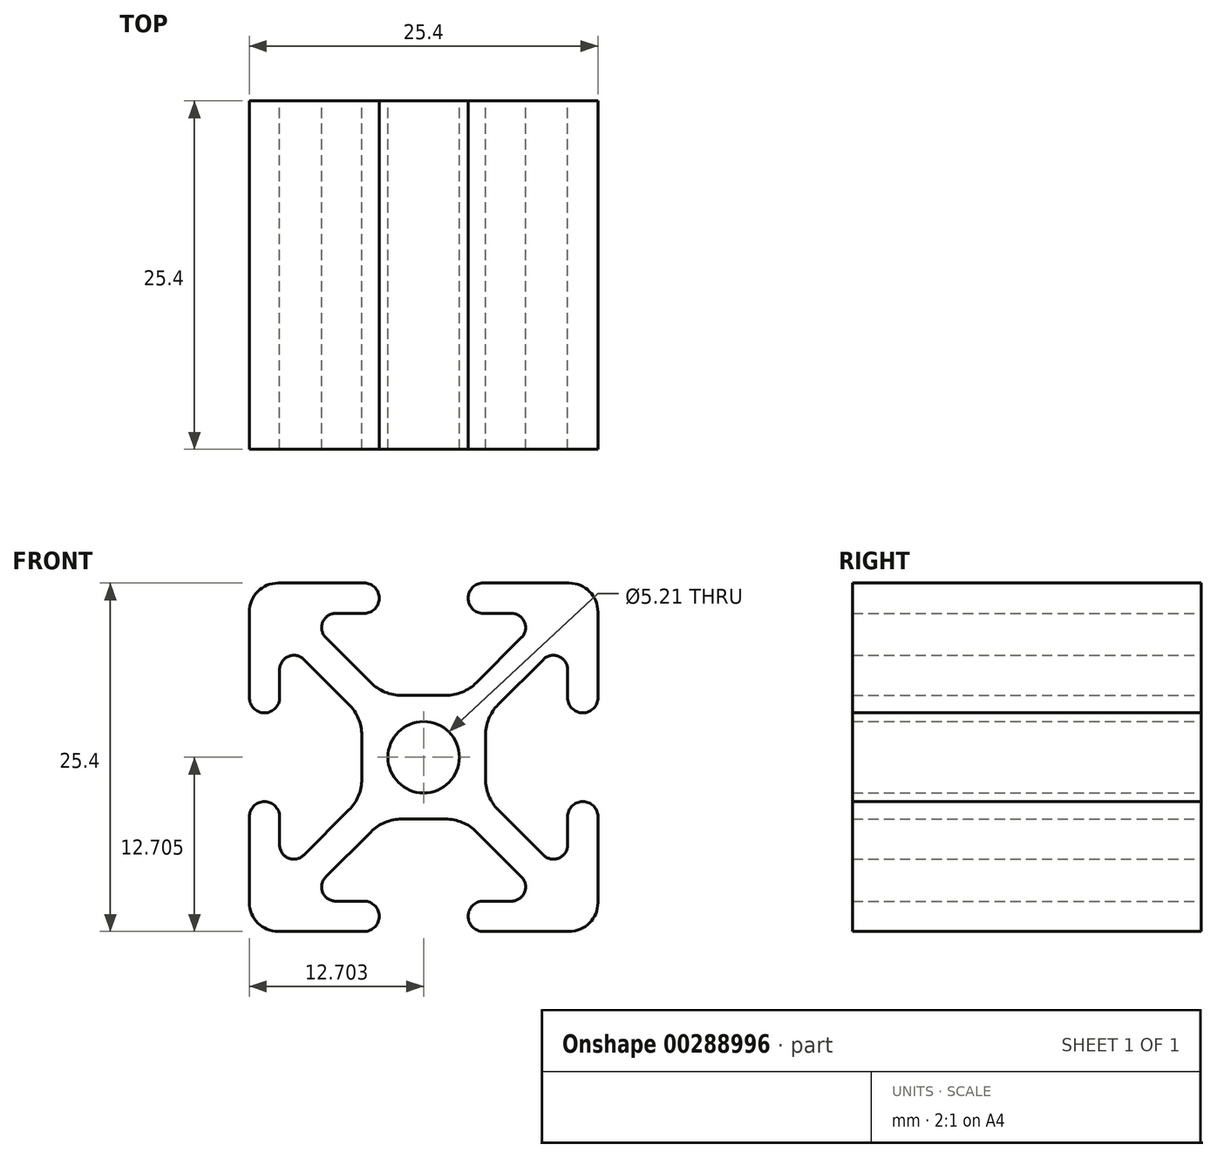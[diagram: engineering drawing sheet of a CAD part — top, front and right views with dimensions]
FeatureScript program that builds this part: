
annotation { "Feature Type Name" : "Feature", "Feature Type Description" : "" }
export const myFeature = defineFeature(function(context is Context, id is Id, definition is map)
    precondition{}
    {
        {
            var Q0;
            Q0=qCreatedBy(makeId("Front.planeOp"),FACE);
            var sketch = newSketch(context, id + "F0", { "sketchPlane" : qUnion([Q0])});
            skArc(sketch, "E0", {"start": v(-10.62, 12.76) * mm, "mid": v(-12.1, 12.15) * mm, "end": v(-12.73, 10.66) * mm});
            skArc(sketch, "E1", {"start": v(-12.73, 4.4) * mm, "mid": v(-11.62, 3.3) * mm, "end": v(-10.52, 4.4) * mm});
            skArc(sketch, "E2", {"start": v(-4.37, 10.55) * mm, "mid": v(-3.27, 11.66) * mm, "end": v(-4.37, 12.76) * mm});
            skArc(sketch, "E3", {"start": v(-8.75, 7.2) * mm, "mid": v(-9.88, 7.42) * mm, "end": v(-10.52, 6.46) * mm});
            skArc(sketch, "E4", {"start": v(-6.43, 10.55) * mm, "mid": v(-7.38, 9.92) * mm, "end": v(-7.16, 8.8) * mm});
            skLineSegment(sketch, "E5", {"start": v(-12.73, 10.66) * mm, "end": v(-12.73, 4.4) * mm});
            skLineSegment(sketch, "E6", {"start": v(-10.62, 12.76) * mm, "end": v(-4.37, 12.76) * mm});
            skLineSegment(sketch, "E7", {"start": v(-10.52, 4.4) * mm, "end": v(-10.52, 6.46) * mm});
            skLineSegment(sketch, "E8", {"start": v(-4.37, 10.55) * mm, "end": v(-6.43, 10.55) * mm});
            skLineSegment(sketch, "E9", {"start": v(-11.51, 7.5) * mm, "end": v(-10.3, 7.5) * mm, "construction": true});
            skLineSegment(sketch, "E10", {"start": v(-13.64, 3.3) * mm, "end": v(-12.36, 3.3) * mm, "construction": true});
            skLineSegment(sketch, "E11", {"start": v(-7.46, 11.03) * mm, "end": v(-7.46, 8.91) * mm, "construction": true});
            skLineSegment(sketch, "E12", {"start": v(-3.27, 12.37) * mm, "end": v(-3.27, 10.25) * mm, "construction": true});
            skLineSegment(sketch, "E13.bottom", {"start": v(1.57, 4.57) * mm, "end": v(-1.63, 4.57) * mm});
            skLineSegment(sketch, "E13.top", {"start": v(1.57, -4.44) * mm, "end": v(-1.63, -4.44) * mm});
            skLineSegment(sketch, "E13.left", {"start": v(4.48, 1.66) * mm, "end": v(4.48, -1.53) * mm});
            skLineSegment(sketch, "E13.right", {"start": v(-4.54, 1.66) * mm, "end": v(-4.54, -1.53) * mm});
            skPoint(sketch, "E13.middle", {"position": v(-0.03, 0.06) * mm});
            skLineSegment(sketch, "E14", {"start": v(-8.75, 7.2) * mm, "end": v(-5.47, 3.9) * mm});
            skLineSegment(sketch, "E15", {"start": v(-7.16, 8.8) * mm, "end": v(-3.87, 5.5) * mm});
            skArc(sketch, "E16.filletArc", {"start": v(-3.87, 5.5) * mm, "mid": v(-2.84, 4.81) * mm, "end": v(-1.63, 4.57) * mm});
            skArc(sketch, "E17.filletArc", {"start": v(-4.54, 1.66) * mm, "mid": v(-4.78, 2.88) * mm, "end": v(-5.47, 3.9) * mm});
            skLineSegment(sketch, "E18", {"start": v(5.32, 0.06) * mm, "end": v(-7.21, 0.06) * mm, "construction": true});
            skPoint(sketch, "E18.startSnap0", {"position": v(2.97, 0.06) * mm});
            skPoint(sketch, "E19", {"position": v(-0.03, -4.44) * mm});
            skLineSegment(sketch, "E20", {"start": v(-0.03, -6.76) * mm, "end": v(-0.03, 5.83) * mm, "construction": true});
            skLineSegment(sketch, "E21.MirrorCS", {"start": v(11.46, 7.5) * mm, "end": v(10.25, 7.5) * mm, "construction": true});
            skArc(sketch, "E22.MirrorCS", {"start": v(10.57, 12.76) * mm, "mid": v(12.06, 12.15) * mm, "end": v(12.67, 10.66) * mm});
            skLineSegment(sketch, "E23.MirrorCS", {"start": v(7.4, 11.03) * mm, "end": v(7.4, 8.91) * mm, "construction": true});
            skLineSegment(sketch, "E24.MirrorCS", {"start": v(10.46, 4.4) * mm, "end": v(10.46, 6.46) * mm});
            skArc(sketch, "E25.MirrorCS", {"start": v(3.82, 5.5) * mm, "mid": v(2.79, 4.81) * mm, "end": v(1.57, 4.57) * mm});
            skLineSegment(sketch, "E26.MirrorCS", {"start": v(8.7, 7.2) * mm, "end": v(5.41, 3.9) * mm});
            skLineSegment(sketch, "E27.MirrorCS", {"start": v(3.21, 12.37) * mm, "end": v(3.21, 10.25) * mm, "construction": true});
            skLineSegment(sketch, "E28.MirrorCS", {"start": v(13.58, 3.3) * mm, "end": v(12.3, 3.3) * mm, "construction": true});
            skArc(sketch, "E29.MirrorCS", {"start": v(4.32, 10.55) * mm, "mid": v(3.21, 11.66) * mm, "end": v(4.32, 12.76) * mm});
            skArc(sketch, "E30.MirrorCS", {"start": v(8.7, 7.2) * mm, "mid": v(9.83, 7.42) * mm, "end": v(10.46, 6.46) * mm});
            skArc(sketch, "E31.MirrorCS", {"start": v(12.67, 4.4) * mm, "mid": v(11.57, 3.3) * mm, "end": v(10.46, 4.4) * mm});
            skLineSegment(sketch, "E32.MirrorCS", {"start": v(10.57, 12.76) * mm, "end": v(4.32, 12.76) * mm});
            skLineSegment(sketch, "E33.MirrorCS", {"start": v(12.67, 10.66) * mm, "end": v(12.67, 4.4) * mm});
            skArc(sketch, "E34.MirrorCS", {"start": v(6.37, 10.55) * mm, "mid": v(7.33, 9.92) * mm, "end": v(7.1, 8.8) * mm});
            skLineSegment(sketch, "E35.MirrorCS", {"start": v(7.1, 8.8) * mm, "end": v(3.82, 5.5) * mm});
            skLineSegment(sketch, "E36.MirrorCS", {"start": v(4.32, 10.55) * mm, "end": v(6.37, 10.55) * mm});
            skArc(sketch, "E37.MirrorCS", {"start": v(4.48, 1.66) * mm, "mid": v(4.72, 2.88) * mm, "end": v(5.41, 3.9) * mm});
            skLineSegment(sketch, "E38.MirrorCS", {"start": v(-11.51, -7.37) * mm, "end": v(-10.3, -7.37) * mm, "construction": true});
            skArc(sketch, "E39.MirrorCS", {"start": v(-3.87, -5.37) * mm, "mid": v(-2.84, -4.69) * mm, "end": v(-1.63, -4.44) * mm});
            skArc(sketch, "E40.MirrorCS", {"start": v(-10.62, -12.64) * mm, "mid": v(-12.1, -12.02) * mm, "end": v(-12.73, -10.53) * mm});
            skArc(sketch, "E41.MirrorCS", {"start": v(-8.75, -7.07) * mm, "mid": v(-9.88, -7.3) * mm, "end": v(-10.52, -6.33) * mm});
            skArc(sketch, "E42.MirrorCS", {"start": v(-6.43, -10.43) * mm, "mid": v(-7.38, -9.79) * mm, "end": v(-7.16, -8.66) * mm});
            skLineSegment(sketch, "E43.MirrorCS", {"start": v(-3.27, -12.24) * mm, "end": v(-3.27, -10.12) * mm, "construction": true});
            skArc(sketch, "E44.MirrorCS", {"start": v(-4.54, -1.53) * mm, "mid": v(-4.78, -2.75) * mm, "end": v(-5.47, -3.78) * mm});
            skLineSegment(sketch, "E45.MirrorCS", {"start": v(-12.73, -10.53) * mm, "end": v(-12.73, -4.28) * mm});
            skLineSegment(sketch, "E46.MirrorCS", {"start": v(-13.64, -3.17) * mm, "end": v(-12.36, -3.17) * mm, "construction": true});
            skLineSegment(sketch, "E47.MirrorCS", {"start": v(-7.46, -10.9) * mm, "end": v(-7.46, -8.78) * mm, "construction": true});
            skLineSegment(sketch, "E48.MirrorCS", {"start": v(-4.37, -10.43) * mm, "end": v(-6.43, -10.43) * mm});
            skLineSegment(sketch, "E49.MirrorCS", {"start": v(-10.62, -12.64) * mm, "end": v(-4.37, -12.64) * mm});
            skLineSegment(sketch, "E50.MirrorCS", {"start": v(-10.52, -4.28) * mm, "end": v(-10.52, -6.33) * mm});
            skArc(sketch, "E51.MirrorCS", {"start": v(-12.73, -4.28) * mm, "mid": v(-11.62, -3.17) * mm, "end": v(-10.52, -4.28) * mm});
            skLineSegment(sketch, "E52.MirrorCS", {"start": v(-8.75, -7.07) * mm, "end": v(-5.47, -3.78) * mm});
            skLineSegment(sketch, "E53.MirrorCS", {"start": v(-7.16, -8.66) * mm, "end": v(-3.87, -5.37) * mm});
            skArc(sketch, "E54.MirrorCS", {"start": v(-4.37, -10.43) * mm, "mid": v(-3.27, -11.53) * mm, "end": v(-4.37, -12.64) * mm});
            skLineSegment(sketch, "E55.MirrorCS", {"start": v(11.46, -7.37) * mm, "end": v(10.25, -7.37) * mm, "construction": true});
            skArc(sketch, "E56.MirrorCS", {"start": v(4.32, -10.43) * mm, "mid": v(3.21, -11.53) * mm, "end": v(4.32, -12.64) * mm});
            skLineSegment(sketch, "E57.MirrorCS", {"start": v(13.58, -3.17) * mm, "end": v(12.3, -3.17) * mm, "construction": true});
            skArc(sketch, "E58.MirrorCS", {"start": v(8.7, -7.07) * mm, "mid": v(9.83, -7.3) * mm, "end": v(10.46, -6.33) * mm});
            skLineSegment(sketch, "E59.MirrorCS", {"start": v(7.1, -8.66) * mm, "end": v(3.82, -5.37) * mm});
            skLineSegment(sketch, "E60.MirrorCS", {"start": v(7.4, -10.9) * mm, "end": v(7.4, -8.78) * mm, "construction": true});
            skLineSegment(sketch, "E61.MirrorCS", {"start": v(3.21, -12.24) * mm, "end": v(3.21, -10.12) * mm, "construction": true});
            skLineSegment(sketch, "E62.MirrorCS", {"start": v(4.32, -10.43) * mm, "end": v(6.37, -10.43) * mm});
            skArc(sketch, "E63.MirrorCS", {"start": v(3.82, -5.37) * mm, "mid": v(2.79, -4.69) * mm, "end": v(1.57, -4.44) * mm});
            skArc(sketch, "E64.MirrorCS", {"start": v(10.57, -12.64) * mm, "mid": v(12.06, -12.02) * mm, "end": v(12.67, -10.53) * mm});
            skLineSegment(sketch, "E65.MirrorCS", {"start": v(10.57, -12.64) * mm, "end": v(4.32, -12.64) * mm});
            skLineSegment(sketch, "E66.MirrorCS", {"start": v(8.7, -7.07) * mm, "end": v(5.41, -3.78) * mm});
            skLineSegment(sketch, "E67.MirrorCS", {"start": v(12.67, -10.53) * mm, "end": v(12.67, -4.28) * mm});
            skArc(sketch, "E68.MirrorCS", {"start": v(12.67, -4.28) * mm, "mid": v(11.57, -3.17) * mm, "end": v(10.46, -4.28) * mm});
            skArc(sketch, "E69.MirrorCS", {"start": v(4.48, -1.53) * mm, "mid": v(4.72, -2.75) * mm, "end": v(5.41, -3.78) * mm});
            skLineSegment(sketch, "E70.MirrorCS", {"start": v(10.46, -4.28) * mm, "end": v(10.46, -6.33) * mm});
            skArc(sketch, "E71.MirrorCS", {"start": v(6.37, -10.43) * mm, "mid": v(7.33, -9.79) * mm, "end": v(7.1, -8.66) * mm});
            skCircle(sketch, "E72", {"center": v(-0.03, 0.06) * mm, "radius": 2.6 * mm});
            skSolve(sketch);
        }
        {
            var Q0;
            Q0 = qSketchRegion(id + "F0", true);
            extrude(context, id + "F1", {"entities" : qUnion([Q0]), "depth" : 25.4 * mm});
        }
    });
